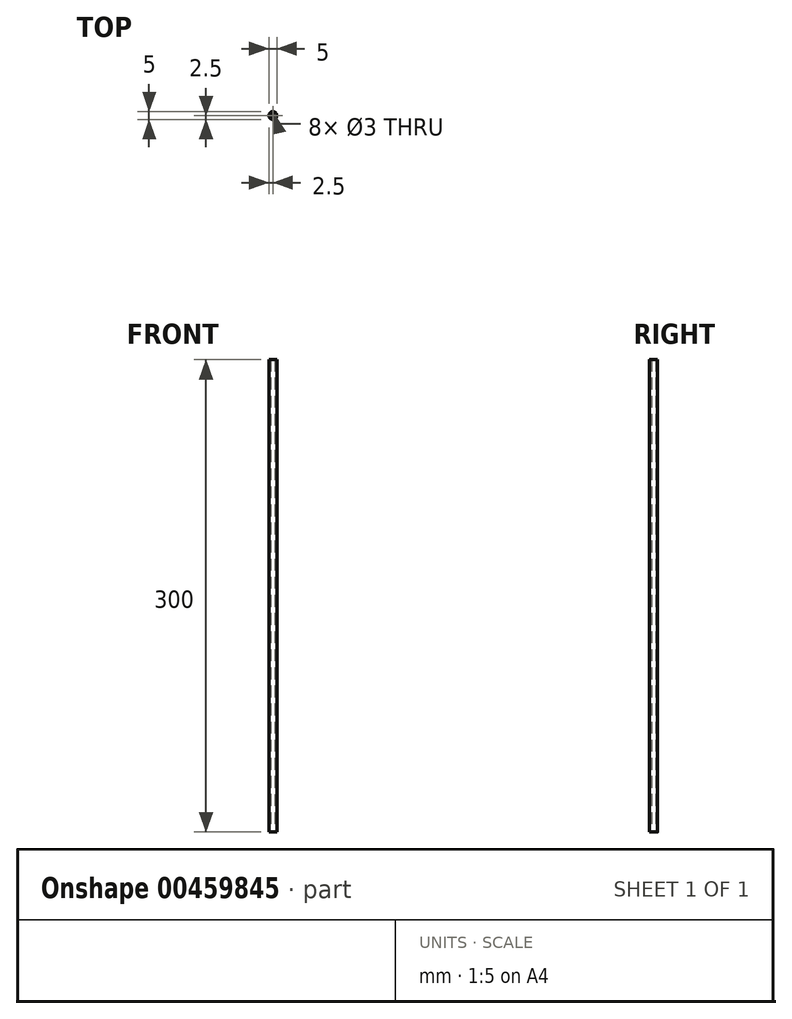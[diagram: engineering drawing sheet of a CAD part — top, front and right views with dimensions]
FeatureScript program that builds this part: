
annotation { "Feature Type Name" : "Feature", "Feature Type Description" : "" }
export const myFeature = defineFeature(function(context is Context, id is Id, definition is map)
    precondition{}
    {
        {
            var Q0;
            Q0=qCreatedBy(makeId("Top.planeOp"),FACE);
            var sketch = newSketch(context, id + "F0", { "sketchPlane" : qUnion([Q0])});
            skCircle(sketch, "E0", {"center": v(0, 0) * mm, "radius": 1.5 * mm});
            skCircle(sketch, "E1", {"center": v(0, 0) * mm, "radius": 2.5 * mm});
            skSolve(sketch);
        }
        {
            var Q0;
            Q0=qSketchRegion(id+"F0",true);
            extrude(context, id + "F1", {"entities" : qUnion([Q0]), "depth" : 300 * mm, "offsetDistance" : 25 * mm});
        }
    });
